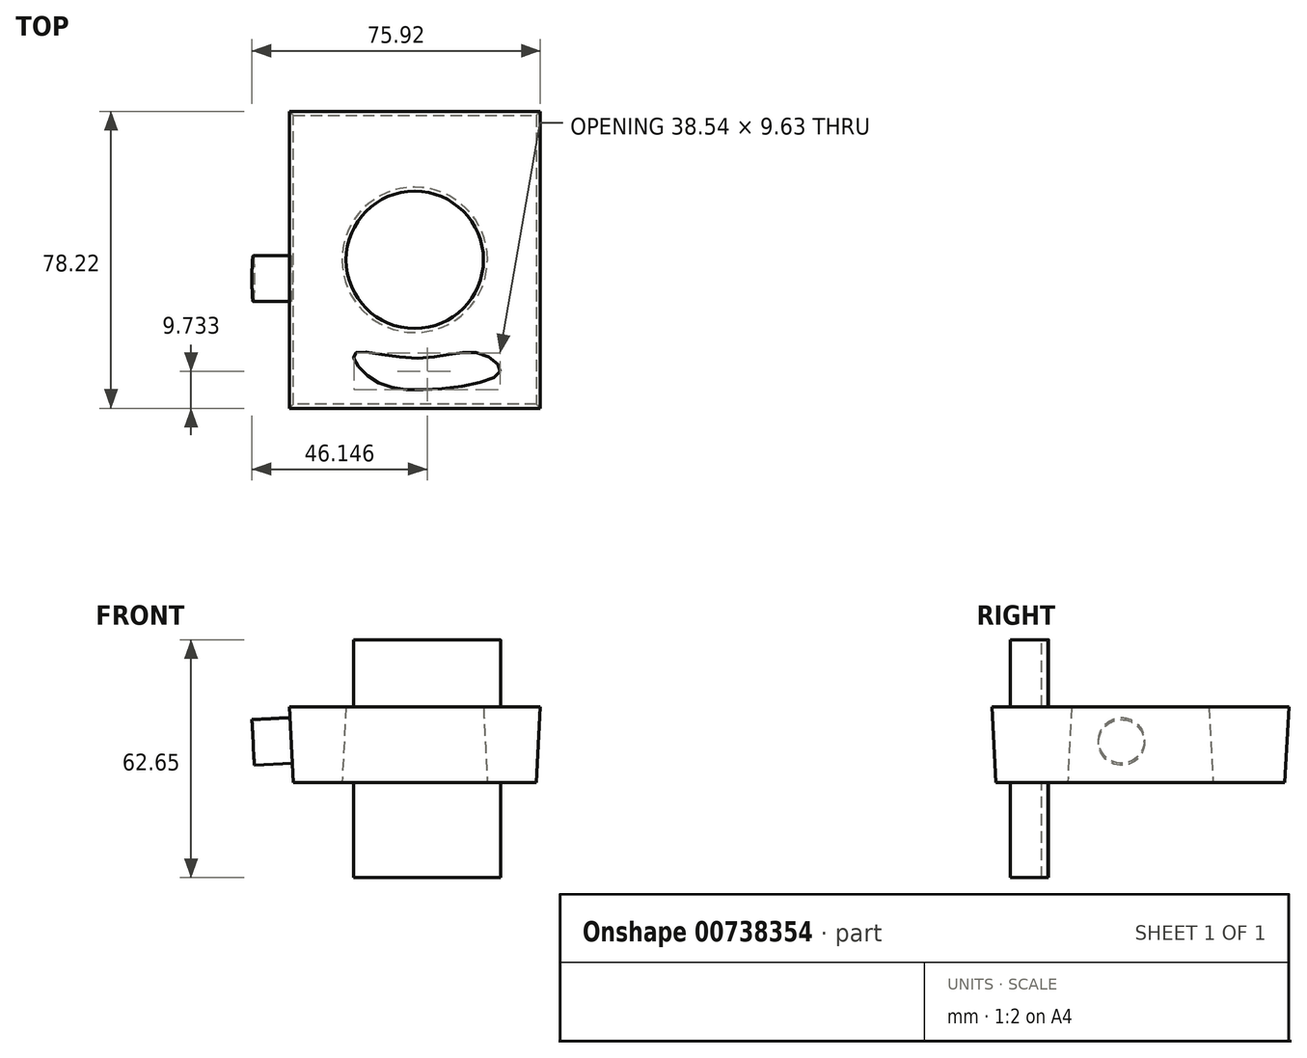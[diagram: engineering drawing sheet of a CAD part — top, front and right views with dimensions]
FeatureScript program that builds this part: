
annotation { "Feature Type Name" : "Feature", "Feature Type Description" : "" }
export const myFeature = defineFeature(function(context is Context, id is Id, definition is map)
    precondition{}
    {
        {
            var Q0;
            Q0=qCreatedBy(makeId("Top.planeOp"),FACE);
            var sketch = newSketch(context, id + "F0", { "sketchPlane" : qUnion([Q0])});
            skLineSegment(sketch, "E0.bottom", {"start": v(32, -38.07) * mm, "end": v(-32, -38.07) * mm});
            skLineSegment(sketch, "E0.top", {"start": v(32, 38.07) * mm, "end": v(-32, 38.07) * mm});
            skLineSegment(sketch, "E0.left", {"start": v(32, -38.07) * mm, "end": v(32, 38.07) * mm});
            skLineSegment(sketch, "E0.right", {"start": v(-32, -38.07) * mm, "end": v(-32, 38.07) * mm});
            skPoint(sketch, "E0.middle", {"position": v(0, 0) * mm});
            skCircle(sketch, "E1", {"center": v(0, 0) * mm, "radius": 19.14 * mm});
            skSolve(sketch);
        }
        {
            var Q0;
            Q0=makeQuery(id+"F0.imprint","IMPRINT",FACE,{"disambiguationData":[TD([[makeQuery(id+"F0.imprint","IMPRINT",EDGE,{"derivedFrom":sQuery(id+"F0.wireOp",EDGE,"E0.bottom")}),-1.0]])]});
            extrude(context, id + "F1", {"entities" : qUnion([Q0]), "depth" : 20 * mm, "offsetDistance" : 25.4 * mm, "hasDraft" : true, "draftAngle" : 3 * degree});
        }
        {
            var Q0;
            Q0=makeQuery(id+"F1.opExtrude","SWEPT_FACE",FACE,{"disambiguationData":[OSD([sQuery(id+"F0.wireOp",EDGE,"E0.right")])]});
            var sketch = newSketch(context, id + "F2", { "sketchPlane" : qUnion([Q0])});
            skCircle(sketch, "E2", {"center": v(4.96, 12.83) * mm, "radius": 6.03 * mm});
            skSolve(sketch);
        }
        {
            var Q0;
            Q0 = qSketchRegion(id + "F2", true);
            extrude(context, id + "F3", {"entities" : qUnion([Q0]), "operationType" : NewBodyOperationType.ADD, "depth" : 10 * mm, "offsetDistance" : 25.4 * mm});
        }
        {
            var Q0;
            Q0=makeQuery(id+"F0.imprint","IMPRINT",FACE,{"disambiguationData":[TD([[makeQuery(id+"F0.imprint","IMPRINT",EDGE,{"derivedFrom":sQuery(id+"F0.wireOp",EDGE,"E0.bottom")}),-1.0]])]});
            var sketch = newSketch(context, id + "F4", { "sketchPlane" : qUnion([Q0])});
            skFitSpline(sketch, "E3", {"points": [v(22.54, -29.36) * mm, v(4.52, -34.08) * mm, v(-11.8, -31.04) * mm, v(-15.88, -24.71) * mm, v(0, -25.95) * mm, v(16.4, -24.53) * mm, v(22.54, -29.36) * mm]});
            skSolve(sketch);
        }
        {
            var Q0;
            Q0 = qSketchRegion(id + "F4", true);
            var Q1;
            Q1=makeQuery(id+"F4.imprint","IMPRINT",FACE,{"disambiguationData":[TD([[makeQuery(id+"F4.imprint","IMPRINT",EDGE,{"derivedFrom":sQuery(id+"F4.wireOp",EDGE,"E3")}),-1.0]])]});
            extrude(context, id + "F5", {"entities" : qUnion([Q0, Q1]), "operationType" : NewBodyOperationType.ADD, "oppositeDirection" : true, "depth" : 25 * mm, "offsetDistance" : 25 * mm, "hasSecondDirection" : true, "secondDirectionOppositeDirection" : false, "secondDirectionDepth" : 37.65 * mm});
        }
    });
